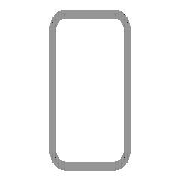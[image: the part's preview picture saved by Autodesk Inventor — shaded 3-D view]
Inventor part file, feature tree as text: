
AUTODESK INVENTOR PART (.ipt)
format: ipt  version: 2025 (Build 290162010, 162A)  size: 129,536 bytes
history: native  units: mm (DEFAULTED — no unit token found)
features: other x3, sketch x1, plane x1
ambient origin geometry x8: Origin, YZ Plane, XZ Plane, XY Plane, X Axis, Y Axis, Z Axis, Center Point
bodies: Solid1 (feature_tree), Body (feature_tree)
feature tree (5):
  other  "Driven Length"
  other  "Start plane"
  other  "End plane"
  sketch  "Sketch3"  dims[d3=1380.0mm d4=0.0mm d7=4.0mm d9=20.0mm d11=40.0mm d12=2.0mm d13=-0.0mm d14=1380.0mm d15=10.0mm d16=20.0mm d17=90.0deg d18=1380.0mm]
  plane  "Work Plane3"
